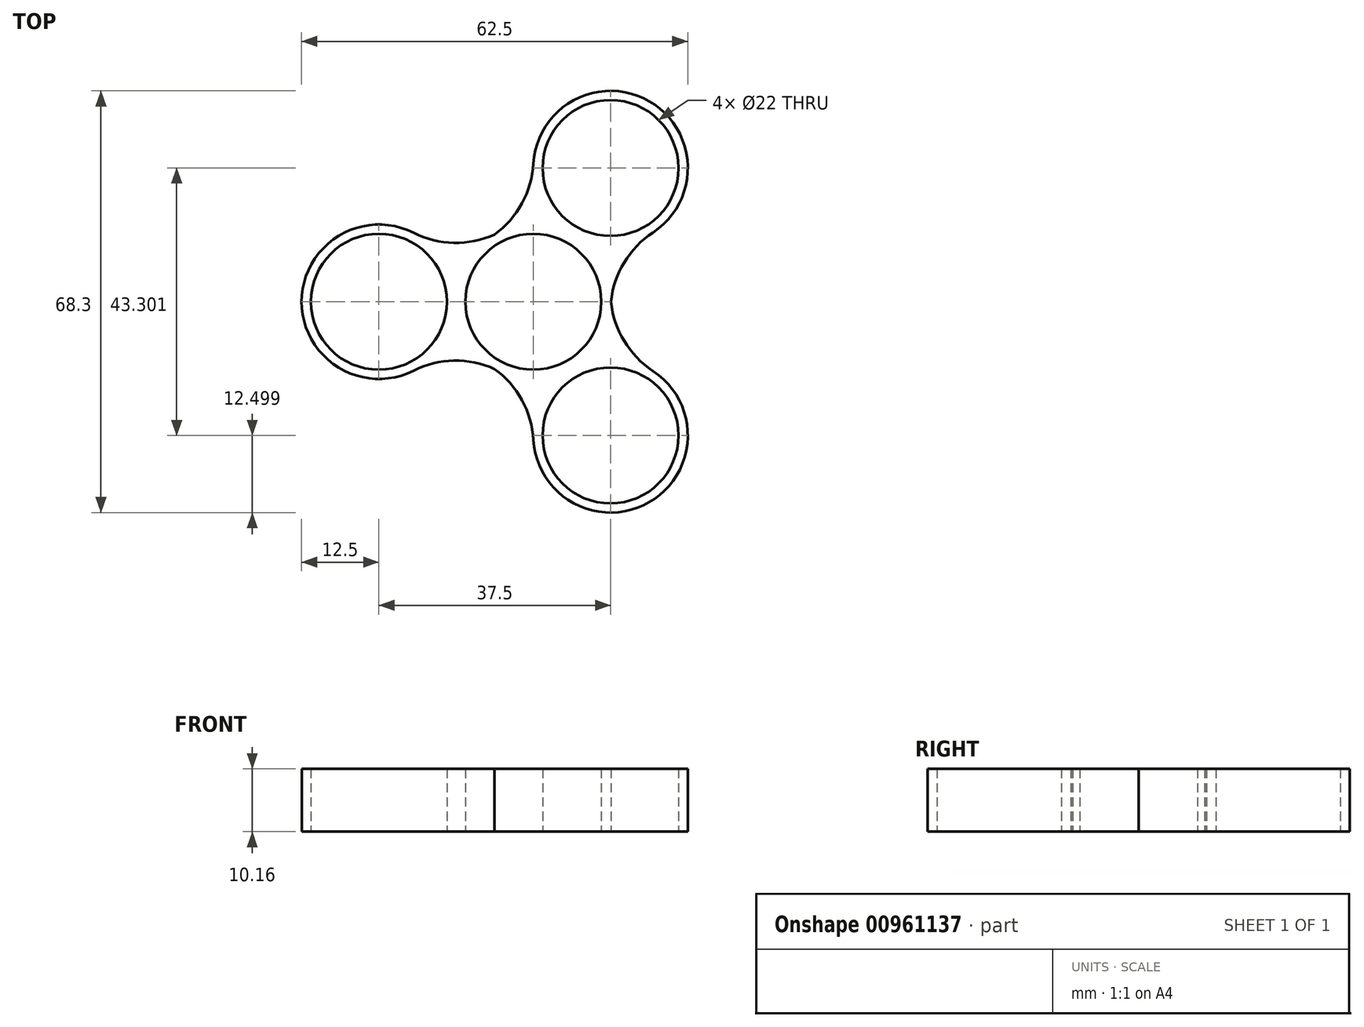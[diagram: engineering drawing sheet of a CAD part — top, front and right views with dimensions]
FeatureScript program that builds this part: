
annotation { "Feature Type Name" : "Feature", "Feature Type Description" : "" }
export const myFeature = defineFeature(function(context is Context, id is Id, definition is map)
    precondition{}
    {
        {
            var Q0;
            Q0=qCreatedBy(makeId("Top.planeOp"),FACE);
            var sketch = newSketch(context, id + "F0", { "sketchPlane" : qUnion([Q0])});
            skCircle(sketch, "E0", {"center": v(0, 0) * mm, "radius": 12.5 * mm});
            skCircle(sketch, "E1.cCircle", {"center": v(0, 0) * mm, "radius": 12.5 * mm, "construction": true});
            skLineSegment(sketch, "E1.0", {"start": v(12.5, 21.65) * mm, "end": v(12.5, -21.65) * mm});
            skLineSegment(sketch, "E1.1", {"start": v(12.5, -21.65) * mm, "end": v(-25, 0) * mm});
            skLineSegment(sketch, "E1.2", {"start": v(-25, 0) * mm, "end": v(12.5, 21.65) * mm});
            skPoint(sketch, "E1.0.midPoint", {"position": v(12.5, 0) * mm});
            skCircle(sketch, "E2", {"center": v(12.5, 21.65) * mm, "radius": 11 * mm});
            skCircle(sketch, "E3", {"center": v(-25, 0) * mm, "radius": 11 * mm});
            skCircle(sketch, "E4", {"center": v(12.5, -21.65) * mm, "radius": 11 * mm});
            skCircle(sketch, "E5", {"center": v(0, 0) * mm, "radius": 11 * mm});
            skCircle(sketch, "E6", {"center": v(-25, 0) * mm, "radius": 12.5 * mm});
            skCircle(sketch, "E7", {"center": v(12.5, 21.65) * mm, "radius": 12.5 * mm});
            skCircle(sketch, "E8", {"center": v(12.5, -21.65) * mm, "radius": 12.5 * mm});
            skSolve(sketch);
        }
        {
            var Q0;
            {var subQ0=sQuery(id+"F0.wireOp",EDGE,"E1.2");var subQ1=sQuery(id+"F0.wireOp",EDGE,"E0");var subQ2=makeQuery(id+"F0.imprint","INTERSECT",VERTEX,{"derivedFrom":[subQ1,subQ0]});Q0=makeQuery(id+"F0.imprint","IMPRINT",FACE,{"disambiguationData":[TD([[makeQuery(id+"F0.imprint","IMPRINT",EDGE,{"disambiguationData":[TD([[subQ2,-1.0]])],"derivedFrom":subQ1}),-1.0]])]});}
            var Q1;
            {var subQ0=sQuery(id+"F0.wireOp",EDGE,"E6");var subQ1=sQuery(id+"F0.wireOp",EDGE,"E1.1");var subQ2=makeQuery(id+"F0.imprint","INTERSECT",VERTEX,{"derivedFrom":[subQ1,subQ0]});Q1=makeQuery(id+"F0.imprint","IMPRINT",FACE,{"disambiguationData":[TD([[makeQuery(id+"F0.imprint","IMPRINT",EDGE,{"disambiguationData":[TD([[subQ2,-1.0]])],"derivedFrom":subQ1}),1.0]])]});}
            var Q2;
            {var subQ0=sQuery(id+"F0.wireOp",EDGE,"E1.0");var subQ1=sQuery(id+"F0.wireOp",EDGE,"E0");var subQ2=makeQuery(id+"F0.imprint","INTERSECT",VERTEX,{"derivedFrom":[subQ1,subQ0]});Q2=makeQuery(id+"F0.imprint","IMPRINT",FACE,{"disambiguationData":[TD([[makeQuery(id+"F0.imprint","IMPRINT",EDGE,{"disambiguationData":[TD([[subQ2,1.0]])],"derivedFrom":subQ1}),-1.0]])]});}
            var Q3;
            {var subQ0=sQuery(id+"F0.wireOp",EDGE,"E8");var subQ1=sQuery(id+"F0.wireOp",EDGE,"E1.0");var subQ2=makeQuery(id+"F0.imprint","INTERSECT",VERTEX,{"derivedFrom":[subQ1,subQ0]});Q3=makeQuery(id+"F0.imprint","IMPRINT",FACE,{"disambiguationData":[TD([[makeQuery(id+"F0.imprint","IMPRINT",EDGE,{"disambiguationData":[TD([[subQ2,-1.0]])],"derivedFrom":subQ1}),1.0]])]});}
            var Q4;
            {var subQ0=sQuery(id+"F0.wireOp",EDGE,"E8");var subQ1=sQuery(id+"F0.wireOp",EDGE,"E1.0");var subQ2=makeQuery(id+"F0.imprint","INTERSECT",VERTEX,{"derivedFrom":[subQ1,subQ0]});Q4=makeQuery(id+"F0.imprint","IMPRINT",FACE,{"disambiguationData":[TD([[makeQuery(id+"F0.imprint","IMPRINT",EDGE,{"disambiguationData":[TD([[subQ2,-1.0]])],"derivedFrom":subQ1}),-1.0]])]});}
            var Q5;
            Q5=makeQuery(id+"F0.imprint","IMPRINT",FACE,{"disambiguationData":[TD([[makeQuery(id+"F0.imprint","IMPRINT",EDGE,{"derivedFrom":sQuery(id+"F0.wireOp",EDGE,"E5")}),-1.0]])]});
            var Q6;
            {var subQ0=sQuery(id+"F0.wireOp",EDGE,"E1.2");var subQ1=sQuery(id+"F0.wireOp",EDGE,"E0");var subQ2=makeQuery(id+"F0.imprint","INTERSECT",VERTEX,{"derivedFrom":[subQ1,subQ0]});Q6=makeQuery(id+"F0.imprint","IMPRINT",FACE,{"disambiguationData":[TD([[makeQuery(id+"F0.imprint","IMPRINT",EDGE,{"disambiguationData":[TD([[subQ2,1.0]])],"derivedFrom":subQ1}),-1.0]])]});}
            var Q7;
            {var subQ0=sQuery(id+"F0.wireOp",EDGE,"E7");var subQ1=sQuery(id+"F0.wireOp",EDGE,"E1.0");var subQ2=makeQuery(id+"F0.imprint","INTERSECT",VERTEX,{"derivedFrom":[subQ1,subQ0]});Q7=makeQuery(id+"F0.imprint","IMPRINT",FACE,{"disambiguationData":[TD([[makeQuery(id+"F0.imprint","IMPRINT",EDGE,{"disambiguationData":[TD([[subQ2,1.0]])],"derivedFrom":subQ1}),-1.0]])]});}
            var Q8;
            {var subQ0=sQuery(id+"F0.wireOp",EDGE,"E7");var subQ1=sQuery(id+"F0.wireOp",EDGE,"E1.0");var subQ2=makeQuery(id+"F0.imprint","INTERSECT",VERTEX,{"derivedFrom":[subQ1,subQ0]});Q8=makeQuery(id+"F0.imprint","IMPRINT",FACE,{"disambiguationData":[TD([[makeQuery(id+"F0.imprint","IMPRINT",EDGE,{"disambiguationData":[TD([[subQ2,1.0]])],"derivedFrom":subQ1}),1.0]])]});}
            var Q9;
            {var subQ0=sQuery(id+"F0.wireOp",EDGE,"E6");var subQ1=sQuery(id+"F0.wireOp",EDGE,"E1.1");var subQ2=makeQuery(id+"F0.imprint","INTERSECT",VERTEX,{"derivedFrom":[subQ1,subQ0]});Q9=makeQuery(id+"F0.imprint","IMPRINT",FACE,{"disambiguationData":[TD([[makeQuery(id+"F0.imprint","IMPRINT",EDGE,{"disambiguationData":[TD([[subQ2,-1.0]])],"derivedFrom":subQ1}),-1.0]])]});}
            extrude(context, id + "F1", {"entities" : qUnion([Q0, Q1, Q2, Q3, Q4, Q5, Q6, Q7, Q8, Q9]), "depth" : 10.16 * mm, "offsetDistance" : 25.4 * mm});
        }
        {
            var Q0;
            Q0=makeQuery(id+"F1.opExtrude","SWEPT_EDGE",EDGE,{"disambiguationData":[OSD([sQuery(id+"F0.wireOp",EDGE,"E1.1"),sQuery(id+"F0.wireOp",EDGE,"E6")])]});
            var Q1;
            Q1=makeQuery(id+"F1.opExtrude","SWEPT_EDGE",EDGE,{"disambiguationData":[OSD([sQuery(id+"F0.wireOp",EDGE,"E1.0"),sQuery(id+"F0.wireOp",EDGE,"E7")])]});
            var Q2;
            Q2=makeQuery(id+"F1.opExtrude","SWEPT_EDGE",EDGE,{"disambiguationData":[OSD([sQuery(id+"F0.wireOp",EDGE,"E1.0"),sQuery(id+"F0.wireOp",EDGE,"E8")])]});
            var Q3;
            Q3=makeQuery(id+"F1.opExtrude","SWEPT_EDGE",EDGE,{"disambiguationData":[OSD([sQuery(id+"F0.wireOp",EDGE,"E1.2"),sQuery(id+"F0.wireOp",EDGE,"E7")])]});
            var Q4;
            Q4=makeQuery(id+"F1.opExtrude","SWEPT_EDGE",EDGE,{"disambiguationData":[OSD([sQuery(id+"F0.wireOp",EDGE,"E1.2"),sQuery(id+"F0.wireOp",EDGE,"E6")])]});
            var Q5;
            Q5=makeQuery(id+"F1.opExtrude","SWEPT_EDGE",EDGE,{"disambiguationData":[OSD([sQuery(id+"F0.wireOp",EDGE,"E1.1"),sQuery(id+"F0.wireOp",EDGE,"E8")])]});
            fillet(context, id + "F2", {"entities" : qUnion([Q0, Q1, Q2, Q3, Q4, Q5]), "tangentPropagation" : true, "radius" : 15.24 * mm, "defaultsChanged" : true, "vertexSettings" : [], "allowEdgeOverflow" : false});
        }
    });
